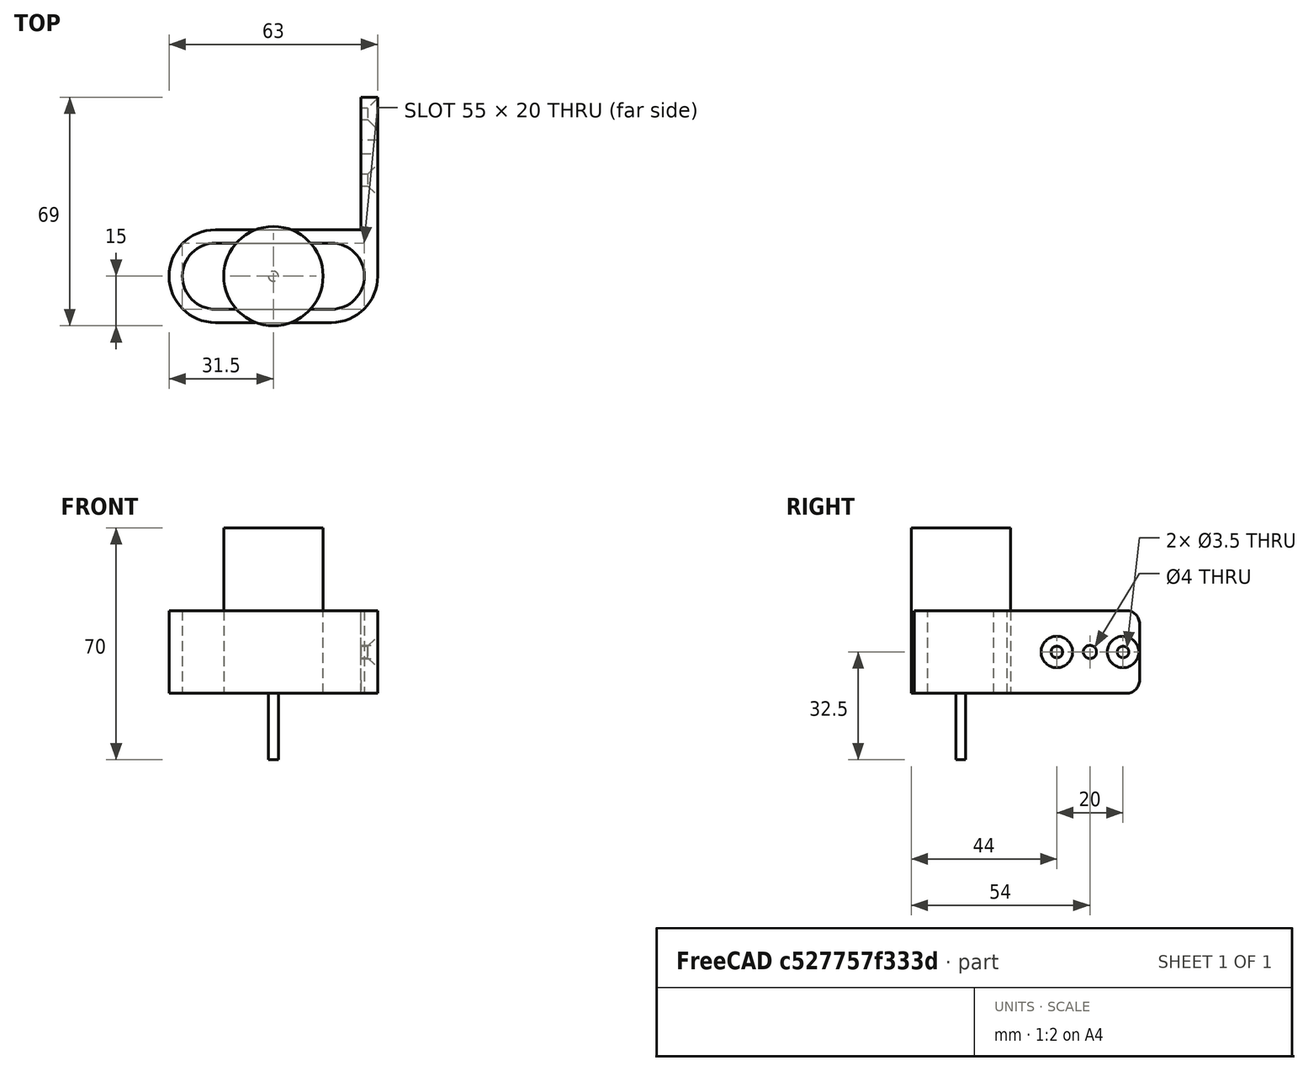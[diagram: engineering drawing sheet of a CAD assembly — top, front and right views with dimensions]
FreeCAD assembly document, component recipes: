
FREECAD ASSEMBLY — COMPONENT RECIPES ("mobile_tester")

This assembly document has 2 components, labeled P0..P1 below (a component is one placed body or linked part). 2 of them carry a construction recipe — the FreeCAD feature program that regenerates the part from scratch, quoted from this document or its linked companion documents; the rest are supplied as boundary geometry only. No exploded tour is included for this assembly.
COMPONENT P0 — recipe-attached ("Part", modeled in this document).
Construction recipe (the document's own serialized feature program — sketch geometry with constraints, then the solid features built on it; lengths are millimeters unless a unit is written):

FEATURE [Sketcher::SketchObject] Sketch
  FullyConstrained = true
  MapMode = 5
  Support = -> [XY_Plane]
  sketch-geometry (11):
    g0: ArcOfCircle CenterX=-17.5 CenterY=0 CenterZ=0 NormalX=0 NormalY=0 NormalZ=1 AngleXU=0 Radius=10 StartAngle=1.5708 EndAngle=4.71239
    g1: ArcOfCircle CenterX=17.5 CenterY=-3e-16 CenterZ=0 NormalX=0 NormalY=0 NormalZ=1 AngleXU=0 Radius=10 StartAngle=4.71239 EndAngle=7.85398
    g2: LineSegment StartX=-17.5 StartY=-10 StartZ=0 EndX=17.5 EndY=-10 EndZ=0
    g3: LineSegment StartX=-17.5 StartY=10 StartZ=0 EndX=17.5 EndY=10 EndZ=0
    g4: ArcOfCircle CenterX=-17.5 CenterY=0 CenterZ=0 NormalX=0 NormalY=0 NormalZ=1 AngleXU=0 Radius=14 StartAngle=1.5708 EndAngle=4.71239
    g5: LineSegment StartX=-17.5 StartY=-14 StartZ=0 EndX=17.5 EndY=-14 EndZ=0
    g6: LineSegment StartX=-17.5 StartY=14 StartZ=0 EndX=26.5 EndY=14 EndZ=0
    g7: LineSegment StartX=31.5 StartY=-3.7e-15 StartZ=0 EndX=31.5 EndY=54 EndZ=0
    g8: LineSegment StartX=26.5 StartY=14 StartZ=0 EndX=26.5 EndY=54 EndZ=0
    g9: ArcOfCircle CenterX=17.5 CenterY=-3e-16 CenterZ=0 NormalX=0 NormalY=0 NormalZ=1 AngleXU=0 Radius=14 StartAngle=4.71239 EndAngle=6.28319
    g10: LineSegment StartX=26.5 StartY=54 StartZ=0 EndX=31.5 EndY=54 EndZ=0
  constraints (29):
    c: Tangent(g0,g3) = 1.5708
    c: Tangent(g0,g2) = -1.5708
    c: Tangent(g2,g1) = -1.5708
    c: Tangent(g3,g1) = 1.5708
    c: Horizontal(g2)
    c: DistanceY(g0,g0) = 20
    c: PointOnObject(g0,g-1)
    c: Symmetric(g0,g1,g-2)
    c: DistanceX(g0,g1) = 35
    c: Tangent(g4,g6) = 1.5708
    c: Tangent(g4,g5) = -1.5708
    c: Horizontal(g5)
    c: PointOnObject(g4,g-1)
    c: DistanceY(g4,g4) = 28
    c: PointOnObject(g7,g-1)
    c: Vertical(g7)
    c: Coincident(g8,g6)
    c: Vertical(g8)
    c: Coincident(g9,g1)
    c: Coincident(g9,g5)
    c: Coincident(g9,g7)
    c: DistanceY(g6,g8) = 40
    c: Horizontal(g6)
    c: DistanceY(g7,g7) = 54
    c: DistanceX(g8,g7) = 5
    c: Coincident(g10,g8)
    c: Coincident(g10,g7)
    c: DistanceX(g4,g5) = 35
    c: DistanceX(g4,g-1) = 17.5
FEATURE [PartDesign::Pad] Pad
  Direction = (1,1,1)
  Length = 25
  Length2 = 100
  Profile = -> Sketch
  Type = 0
FEATURE [PartDesign::Fillet] Fillet
  Base = -> Pad [Edge20,Edge21]
  BaseFeature = -> Pad
  Radius = 4
  SupportTransform = false
FEATURE [Sketcher::SketchObject] Sketch001
  ExternalGeometry = -> [Fillet]
  FullyConstrained = true
  MapMode = 5
  Placement = pos=(31.5,0,0) rot=(0.57735,0.57735,0.57735;2.0944rad)
  Support = -> [Fillet]
  sketch-geometry (3):
    g0: Circle CenterX=39 CenterY=12.5 CenterZ=0 NormalX=0 NormalY=0 NormalZ=1 AngleXU=0 Radius=2
    g1: Circle CenterX=49 CenterY=12.5 CenterZ=0 NormalX=0 NormalY=0 NormalZ=1 AngleXU=0 Radius=1.75
    g2: Circle CenterX=29 CenterY=12.5 CenterZ=0 NormalX=0 NormalY=0 NormalZ=1 AngleXU=0 Radius=1.75
  constraints (9):
    c: Equal(g2,g1)
    c: Diameter(g1) = 3.5
    c: DistanceY(g-1,g2) = 12.5
    c: DistanceY(g-1,g1) = 12.5
    c: DistanceX(g1,g-3) = 5
    c: DistanceX(g2,g1) = 20
    c: DistanceY(g-1,g0) = 12.5
    c: DistanceX(g2,g0) = 10
    c: Diameter(g0) = 4
FEATURE [PartDesign::Pocket] Pocket
  BaseFeature = -> Fillet
  Length = 5
  Length2 = 100
  Profile = -> Sketch001
  Type = 1
FEATURE [PartDesign::Chamfer] Chamfer
  Angle = 45
  Base = -> Pocket [Edge36]
  BaseFeature = -> Pocket
  ChamferType = 0
  FlipDirection = false
  Size = 3
  Size2 = 1
  SupportTransform = false
FEATURE [PartDesign::Chamfer] Chamfer001
  Angle = 45
  Base = -> Chamfer [Edge21]
  BaseFeature = -> Chamfer
  ChamferType = 0
  FlipDirection = false
  Size = 3
  Size2 = 1
  SupportTransform = false
FEATURE [PartDesign::Body] Body
  Group = -> [Sketch,Pad,Fillet,Sketch001,Pocket,Chamfer,Chamfer001]
  Origin = -> Origin
  Tip = -> Chamfer001
COMPONENT P1 — recipe-attached ("motor", modeled in this document).
Construction recipe (the document's own serialized feature program — sketch geometry with constraints, then the solid features built on it; lengths are millimeters unless a unit is written):

FEATURE [PartDesign::CoordinateSystem] LCS_0003
  AttacherType = Attacher::AttachEngine3D
  MapMode = 2
  Support = -> [X_Axis005]
FEATURE [Sketcher::SketchObject] Sketch_1
  FullyConstrained = true
  sketch-geometry (1):
    g0: Circle CenterX=0 CenterY=0 CenterZ=0 NormalX=0 NormalY=0 NormalZ=1 AngleXU=0 Radius=15
  constraints (2):
    c: Coincident(g0,g-1)
    c: Diameter(g0) = 30
FEATURE [PartDesign::Pad] Pad001
  Direction = (1,1,1)
  Length = 50
  Length2 = 100
  Profile = -> Sketch_1
  Type = 0
FEATURE [Sketcher::SketchObject] Sketch002
  FullyConstrained = true
  MapMode = 5
  Placement = pos=(0,0,0) rot=(1,0,0;3.14159rad)
  Support = -> [Pad001]
  sketch-geometry (1):
    g0: Circle CenterX=0 CenterY=0 CenterZ=0 NormalX=0 NormalY=0 NormalZ=1 AngleXU=0 Radius=1.5
  constraints (2):
    c: Coincident(g0,g-1)
    c: Diameter(g0) = 3
FEATURE [PartDesign::Pad] Pad002
  BaseFeature = -> Pad001
  Direction = (1,1,1)
  Length = 20
  Length2 = 100
  Profile = -> Sketch002
  Type = 0
FEATURE [PartDesign::Body] Body_2
  Group = -> [LCS_0003,Sketch_1,Pad001,Sketch002,Pad002]
  Origin = -> Origin005
  Tip = -> Pad002
PROVENANCE & LICENSES
A FreeCAD (.FCStd) document from a public repository crawl; recipes are the document's own serialized feature recipes (and, for linked parts, companion documents' recipes).
License: as declared in the source repository (recorded in the dataset sidecar).
